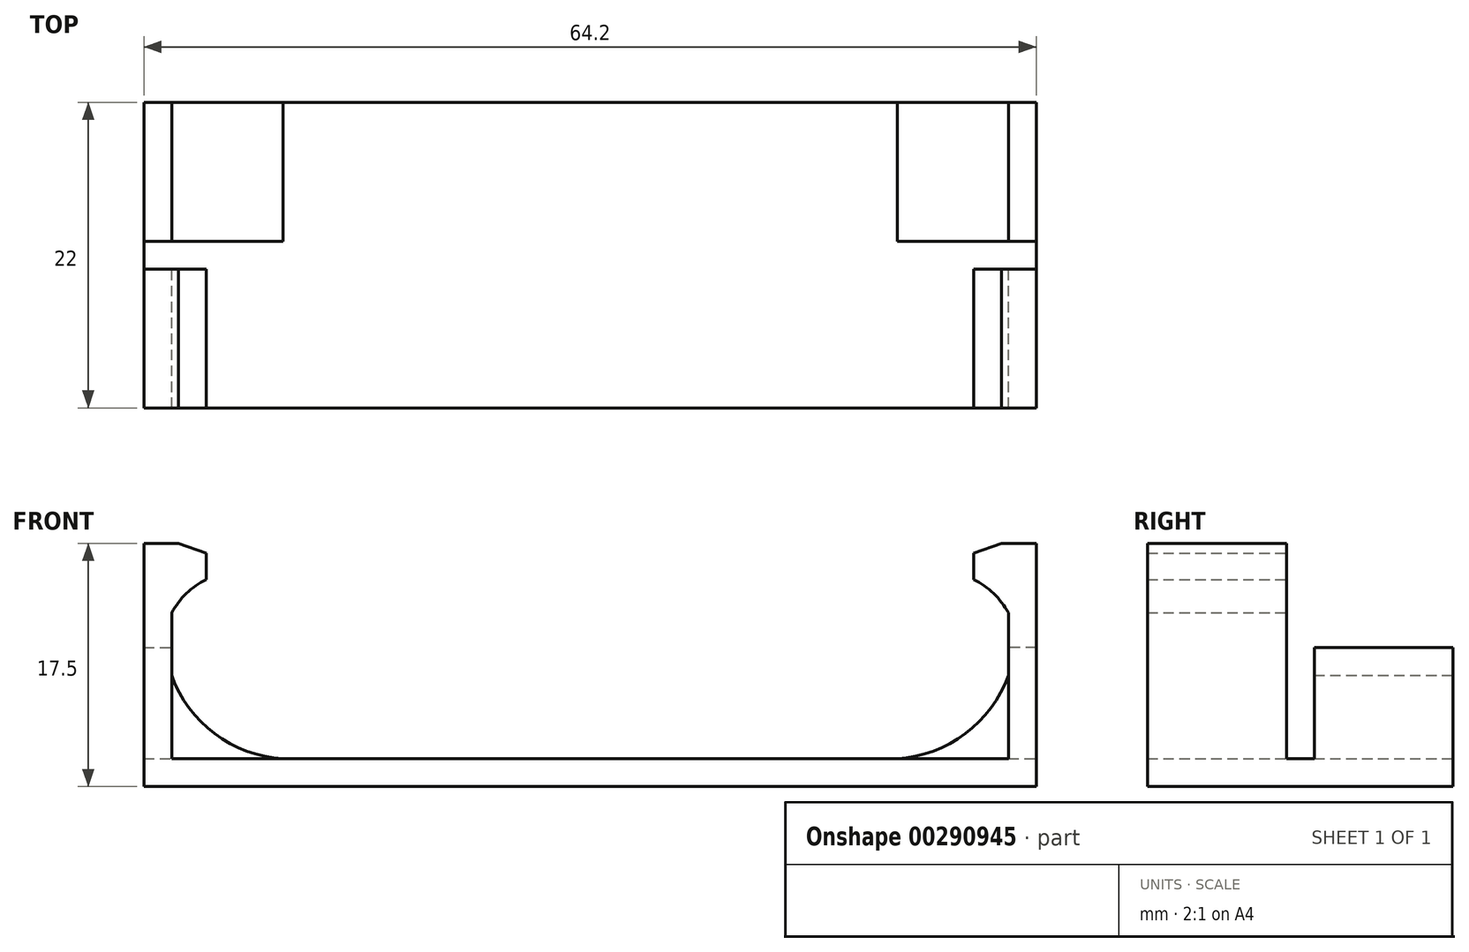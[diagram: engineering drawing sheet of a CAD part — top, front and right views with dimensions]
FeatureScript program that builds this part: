
annotation { "Feature Type Name" : "Feature", "Feature Type Description" : "" }
export const myFeature = defineFeature(function(context is Context, id is Id, definition is map)
    precondition{}
    {
        {
            var Q0;
            Q0=qCreatedBy(makeId("Front.planeOp"),FACE);
            var sketch = newSketch(context, id + "F0", { "sketchPlane" : qUnion([Q0])});
            skLineSegment(sketch, "E0", {"start": v(0, 0) * mm, "end": v(0, 17.5) * mm});
            skLineSegment(sketch, "E1", {"start": v(0, 0) * mm, "end": v(64.2, 0) * mm});
            skLineSegment(sketch, "E2", {"start": v(64.2, 0) * mm, "end": v(64.2, 17.5) * mm});
            skLineSegment(sketch, "E3", {"start": v(64.2, 17.5) * mm, "end": v(61.7, 17.5) * mm});
            skLineSegment(sketch, "E4", {"start": v(0, 17.5) * mm, "end": v(2.5, 17.5) * mm});
            skLineSegment(sketch, "E5.bottom", {"start": v(2, 2) * mm, "end": v(62.2, 2) * mm});
            skLineSegment(sketch, "E5.left", {"start": v(2, 2) * mm, "end": v(2, 12.5) * mm});
            skLineSegment(sketch, "E5.right", {"start": v(62.2, 2) * mm, "end": v(62.2, 12.5) * mm});
            skArc(sketch, "E6", {"start": v(4.5, 14.9) * mm, "mid": v(3.06, 13.9) * mm, "end": v(2, 12.5) * mm});
            skLineSegment(sketch, "E7", {"start": v(2.5, 17.5) * mm, "end": v(4.5, 16.79) * mm});
            skLineSegment(sketch, "E8", {"start": v(4.5, 16.79) * mm, "end": v(4.5, 14.9) * mm});
            skLineSegment(sketch, "E9.MirrorCS", {"start": v(59.7, 16.79) * mm, "end": v(59.7, 14.9) * mm});
            skArc(sketch, "E10.MirrorCS", {"start": v(59.7, 14.9) * mm, "mid": v(61.14, 13.9) * mm, "end": v(62.2, 12.5) * mm});
            skLineSegment(sketch, "E11.MirrorCS", {"start": v(61.7, 17.5) * mm, "end": v(59.7, 16.79) * mm});
            skLineSegment(sketch, "E12", {"start": v(2, 2) * mm, "end": v(0, 2) * mm});
            skLineSegment(sketch, "E13", {"start": v(0, 2) * mm, "end": v(64.2, 2) * mm});
            skSolve(sketch);
        }
        {
            var Q0;
            Q0=makeQuery(id+"F0.imprint","IMPRINT",FACE,{"disambiguationData":[TD([[makeQuery(id+"F0.imprint","IMPRINT",EDGE,{"derivedFrom":sQuery(id+"F0.wireOp",EDGE,"E0")}),-1.0]])]});
            var Q1;
            {var subQ1=sQuery(id+"F0.wireOp",EDGE,"E3");Q1=makeQuery(id+"F0.imprint","IMPRINT",FACE,{"disambiguationData":[TD([[makeQuery(id+"F0.imprint","IMPRINT",EDGE,{"derivedFrom":subQ1}),1.0]])]});}
            var Q2;
            {var subQ1=sQuery(id+"F0.wireOp",EDGE,"E4");Q2=makeQuery(id+"F0.imprint","IMPRINT",FACE,{"disambiguationData":[TD([[makeQuery(id+"F0.imprint","IMPRINT",EDGE,{"derivedFrom":subQ1}),-1.0]])]});}
            extrude(context, id + "F1", {"entities" : qUnion([Q0, Q1, Q2]), "depth" : 10 * mm});
        }
        {
            var Q0;
            {var subQ1=sQuery(id+"F0.wireOp",EDGE,"E1");Q0=makeQuery(id+"F0.imprint","IMPRINT",FACE,{"disambiguationData":[TD([[makeQuery(id+"F0.imprint","IMPRINT",EDGE,{"derivedFrom":subQ1}),1.0]])]});}
            extrude(context, id + "F2", {"entities" : qUnion([Q0]), "operationType" : NewBodyOperationType.ADD, "oppositeDirection" : true, "depth" : 12 * mm});
        }
        {
            var Q0;
            Q0=makeQuery(id+"F2.opExtrude","CAP_FACE",FACE,{"disambiguationData":[OSD([sQuery(id+"F0.wireOp",EDGE,"E0"),sQuery(id+"F0.wireOp",EDGE,"E1"),sQuery(id+"F0.wireOp",EDGE,"E2"),sQuery(id+"F0.wireOp",EDGE,"E13")])],"isStart":false});
            var sketch = newSketch(context, id + "F3", { "sketchPlane" : qUnion([Q0])});
            skLineSegment(sketch, "E14", {"start": v(0, 2) * mm, "end": v(0, 10) * mm});
            skLineSegment(sketch, "E15", {"start": v(0, 10) * mm, "end": v(-2, 10) * mm});
            skLineSegment(sketch, "E16", {"start": v(-2, 10) * mm, "end": v(-2, 8) * mm});
            skLineSegment(sketch, "E17", {"start": v(0, 2) * mm, "end": v(-10, 2) * mm});
            skArc(sketch, "E18", {"start": v(-10, 2) * mm, "mid": v(-5.1, 3.8) * mm, "end": v(-2, 8) * mm});
            skLineSegment(sketch, "E19", {"start": v(-64.2, 2) * mm, "end": v(-64.2, 10) * mm});
            skArc(sketch, "E20.MirrorCS", {"start": v(-54.2, 2) * mm, "mid": v(-59.1, 3.8) * mm, "end": v(-62.2, 8) * mm});
            skLineSegment(sketch, "E21.MirrorCS", {"start": v(-62.2, 10) * mm, "end": v(-62.2, 8) * mm});
            skLineSegment(sketch, "E22.MirrorCS", {"start": v(-64.2, 10) * mm, "end": v(-62.2, 10) * mm});
            skLineSegment(sketch, "E23.MirrorCS", {"start": v(-64.2, 2) * mm, "end": v(-54.2, 2) * mm});
            skSolve(sketch);
        }
        {
            var Q0;
            Q0=makeQuery(id+"F3.imprint","IMPRINT",FACE,{"disambiguationData":[TD([[makeQuery(id+"F3.imprint","IMPRINT",EDGE,{"derivedFrom":sQuery(id+"F3.wireOp",EDGE,"E19")}),-1.0]])]});
            var Q1;
            Q1=makeQuery(id+"F3.imprint","IMPRINT",FACE,{"disambiguationData":[TD([[makeQuery(id+"F3.imprint","IMPRINT",EDGE,{"derivedFrom":sQuery(id+"F3.wireOp",EDGE,"E14")}),1.0]])]});
            extrude(context, id + "F4", {"entities" : qUnion([Q0, Q1]), "operationType" : NewBodyOperationType.ADD, "oppositeDirection" : true, "depth" : 10 * mm});
        }
    });
